# Revit family: Faucet-Two_Handle-American_Standard-Delancey-70522XX_Series
name_source: partatom
category: Plumbing Fixtures
revit_build: Autodesk Revit 2014 (Build: 20130308_1515(x64)
units: mm (PartAtom-declared; Revit-internal decimal feet)

## types (5) — shared parameters
ADA Compliant = Yes
Assembly Code = D2020300
CW Connection = Yes
CWFU = 1.5
Cold Water Connection Diameter = 1/2"
Default Elevation = 0"
Description = Fluent Two-Handle Centerset Lavatory Faucet.
Flow Rate = 1.2 gpm (4.5 L/min)
HW Connection = Yes
HWFU = 1.5
Height = 8"
Hot Water Connection Diameter = 1/2"
Installation Type = Deck Mounted
Length = 4 13/16"
Manufacturer = American Standard
Price = Prices may vary. Please consult Manufacturer Representative for most up-to-date price list.
URL = http://www.americanstandard-us.com
Vent Connection = No
WFU = 2
Warranty Information = Limited Lifetime Warranty
Waste Connection = No
Width = 10 5/16"

## per-type parameters (varying)
| type | Finish | Material | Pop-Up Drain | Temperature Indicators |
| 7052207.002 | Metal-American Standard-002-Polished Chrome | Metal-American Standard-002-Polished Chrome | Yes | No |
| 7052207.295 | Metal-American Standard-295-Brushed Nickel | Metal-American Standard-295-Brushed Nickel | Yes | No |
| 7052207.013 | Metal-American Standard-013-Polished Nickel | Metal-American Standard-013-Polished Nickel | Yes | No |
| 7052207.278 | Metal-American Standard-278-Legacy Bronze | Metal-American Standard-278-Legacy Bronze | Yes | No |
| 7052214.002 | Metal-American Standard-002-Polished Chrome | Metal-American Standard-002-Polished Chrome | No | Yes |

note: column(s) folded — value = type name in every type: Model

## geometry (parser evidence)
native form markers: Sweep x1
no freeform markers — native parametric forms only
